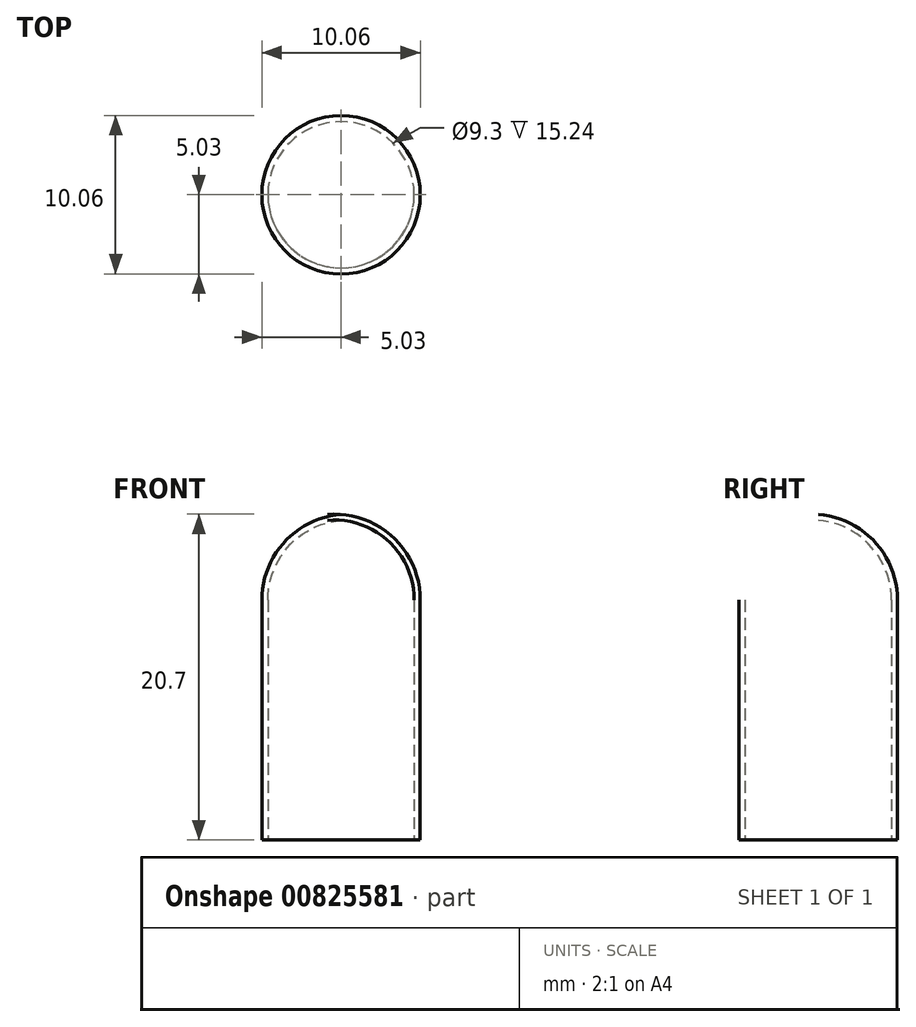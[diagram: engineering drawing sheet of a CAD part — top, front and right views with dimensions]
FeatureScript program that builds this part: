
annotation { "Feature Type Name" : "Feature", "Feature Type Description" : "" }
export const myFeature = defineFeature(function(context is Context, id is Id, definition is map)
    precondition{}
    {
        {
            var Q0;
            Q0=qCreatedBy(makeId("Front.planeOp"),FACE);
            var sketch = newSketch(context, id + "F0", { "sketchPlane" : qUnion([Q0])});
            skLineSegment(sketch, "E0", {"start": v(-0.43, 15.24) * mm, "end": v(0, 15.24) * mm});
            skLineSegment(sketch, "E1", {"start": v(4.65, 15.24) * mm, "end": v(4.65, 0) * mm});
            skLineSegment(sketch, "E2", {"start": v(4.65, 0) * mm, "end": v(5.03, 0) * mm});
            skLineSegment(sketch, "E3", {"start": v(5.03, 0) * mm, "end": v(5.03, 15.24) * mm});
            skLineSegment(sketch, "E4", {"start": v(5.03, 15.24) * mm, "end": v(4.65, 15.24) * mm});
            skArc(sketch, "E5", {"start": v(5.03, 15.24) * mm, "mid": v(3.58, 18.95) * mm, "end": v(0, 20.68) * mm});
            skArc(sketch, "E6", {"start": v(4.65, 15.24) * mm, "mid": v(3.3, 18.68) * mm, "end": v(0, 20.3) * mm});
            skLineSegment(sketch, "E7", {"start": v(0, 0) * mm, "end": v(0, 16.67) * mm, "construction": true});
            skLineSegment(sketch, "E8", {"start": v(0, 20.3) * mm, "end": v(0, 20.68) * mm});
            skPoint(sketch, "E8.startSnap0", {"position": v(-0.86, 20.3) * mm});
            skLineSegment(sketch, "E9", {"start": v(0, 20.68) * mm, "end": v(0, 20.3) * mm});
            skLineSegment(sketch, "E10.trimOffspring", {"start": v(0, 15.24) * mm, "end": v(-0.43, 15.24) * mm});
            skSolve(sketch);
        }
        {
            var Q0;
            {var subQ0=sQuery(id+"F0.wireOp",EDGE,"Knnb8tRt-JJSC-GeLf-JICp-eAvEMYMsdSDj");Q0=makeQuery(id+"F0.imprint","IMPRINT",FACE,{"disambiguationData":[TD([[makeQuery(id+"F0.imprint","IMPRINT",EDGE,{"derivedFrom":subQ0}),1.0]])]});}
            var Q1;
            {var subQ2=sQuery(id+"F0.wireOp",EDGE,"E5");Q1=makeQuery(id+"F0.imprint","IMPRINT",FACE,{"disambiguationData":[TD([[makeQuery(id+"F0.imprint","IMPRINT",EDGE,{"derivedFrom":subQ2}),1.0]])]});}
            var Q2;
            {var subQ0=sQuery(id+"F0.wireOp",EDGE,"E1");Q2=makeQuery(id+"F0.imprint","IMPRINT",FACE,{"disambiguationData":[TD([[makeQuery(id+"F0.imprint","IMPRINT",EDGE,{"derivedFrom":subQ0}),1.0]])]});}
            var Q3;
            Q3=sQuery(id+"F0.wireOp",EDGE,"E7");
            revolve(context, id + "F1", {"surfaceOperationType" : NewSurfaceOperationType.NEW, "entities" : qUnion([Q0, Q1, Q2]), "axis" : qUnion([Q3]), "revolveType" : RevolveType.FULL});
        }
    });
